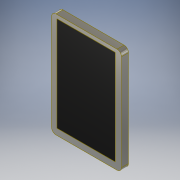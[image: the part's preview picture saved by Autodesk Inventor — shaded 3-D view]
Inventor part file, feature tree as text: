
AUTODESK INVENTOR PART (.ipt)
format: ipt  version: 2018 (Build 220112000, 112)  size: 115,200 bytes
history: native  units: in
note: dims shown in document units (in); Inventor stores cm internally (conversion verified against a paired STEP export)
features: extrude x2, sketch x2
ambient origin geometry x8: Origin, YZ Plane, XZ Plane, XY Plane, X Axis, Y Axis, Z Axis, Center Point
bodies: Solid1 (feature_tree)
feature tree (4):
  extrude  "Extrusion1"  Depth=3.0in
  extrude  "Extrusion2"  Depth=0.2in TaperAngle=0.0deg
  sketch  "Sketch1"  dims[d0=2.0in d1=3.0in]
  sketch  "Sketch2"  dims[d2=0.125in d3=0.2in d4=0.0in d5=0.001in d6=0.0in]
